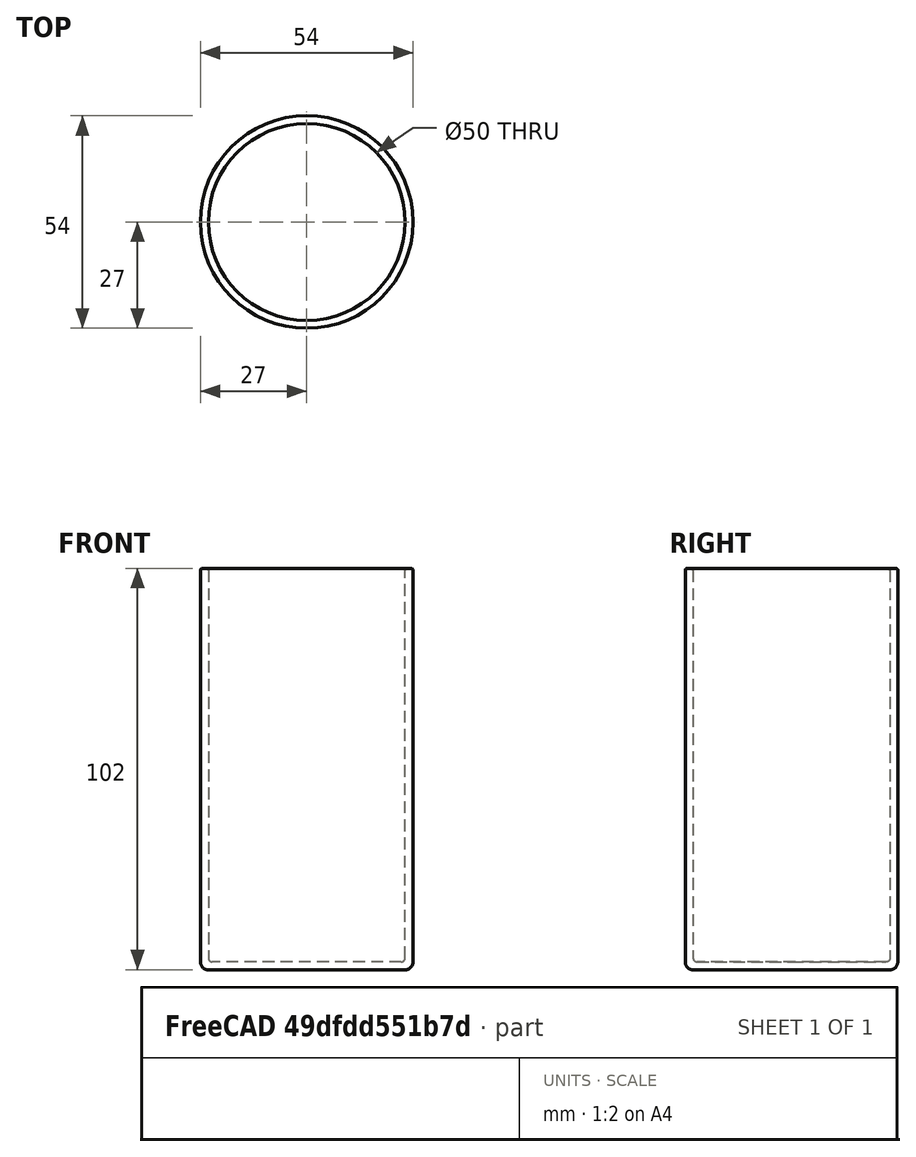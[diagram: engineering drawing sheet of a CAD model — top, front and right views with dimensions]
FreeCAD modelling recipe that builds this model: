
FCSTD DOCUMENT  (FreeCAD 0.21R33668 +26 (Git))
Label: Pencil Cup
License: All rights reserved
LicenseURL: https://en.wikipedia.org/wiki/All_rights_reserved
objects: PartDesign::Fillet×2, Part::Cylinder×1, Part::Thickness×1, PartDesign::FeatureBase×1, PartDesign::Body×1
note: 8 computed .brp shape members not serialized (recipe doc carries the construction recipe); baked Part::Feature solids carry a one-line shape summary decoded from their .brp

FEATURE [Part::Cylinder] Cylinder
  Angle = 360
  AttacherType = Attacher::AttachEngine3D
  FirstAngle = 0
  Height = 100
  Radius = 25
  SecondAngle = 0
FEATURE [Part::Thickness] Thickness
  Faces = -> Cylinder [Face3]
  Intersection = false
  Join = 0
  Mode = 0
  SelfIntersection = false
  Value = 2
FEATURE [PartDesign::FeatureBase] BaseFeature
  BaseFeature = -> Thickness
FEATURE [PartDesign::Fillet] Fillet
  Base = -> BaseFeature [Edge4,Edge3]
  BaseFeature = -> BaseFeature
  Radius = 0.5
  SupportTransform = false
  UseAllEdges = false
FEATURE [PartDesign::Fillet] Fillet001
  Base = -> Fillet [Edge3]
  BaseFeature = -> Fillet
  Radius = 1
  SupportTransform = false
  UseAllEdges = false
FEATURE [PartDesign::Body] Body
  BaseFeature = -> Thickness
  Group = -> [BaseFeature,Fillet,Fillet001]
  Origin = -> Origin
  Tip = -> Fillet001
